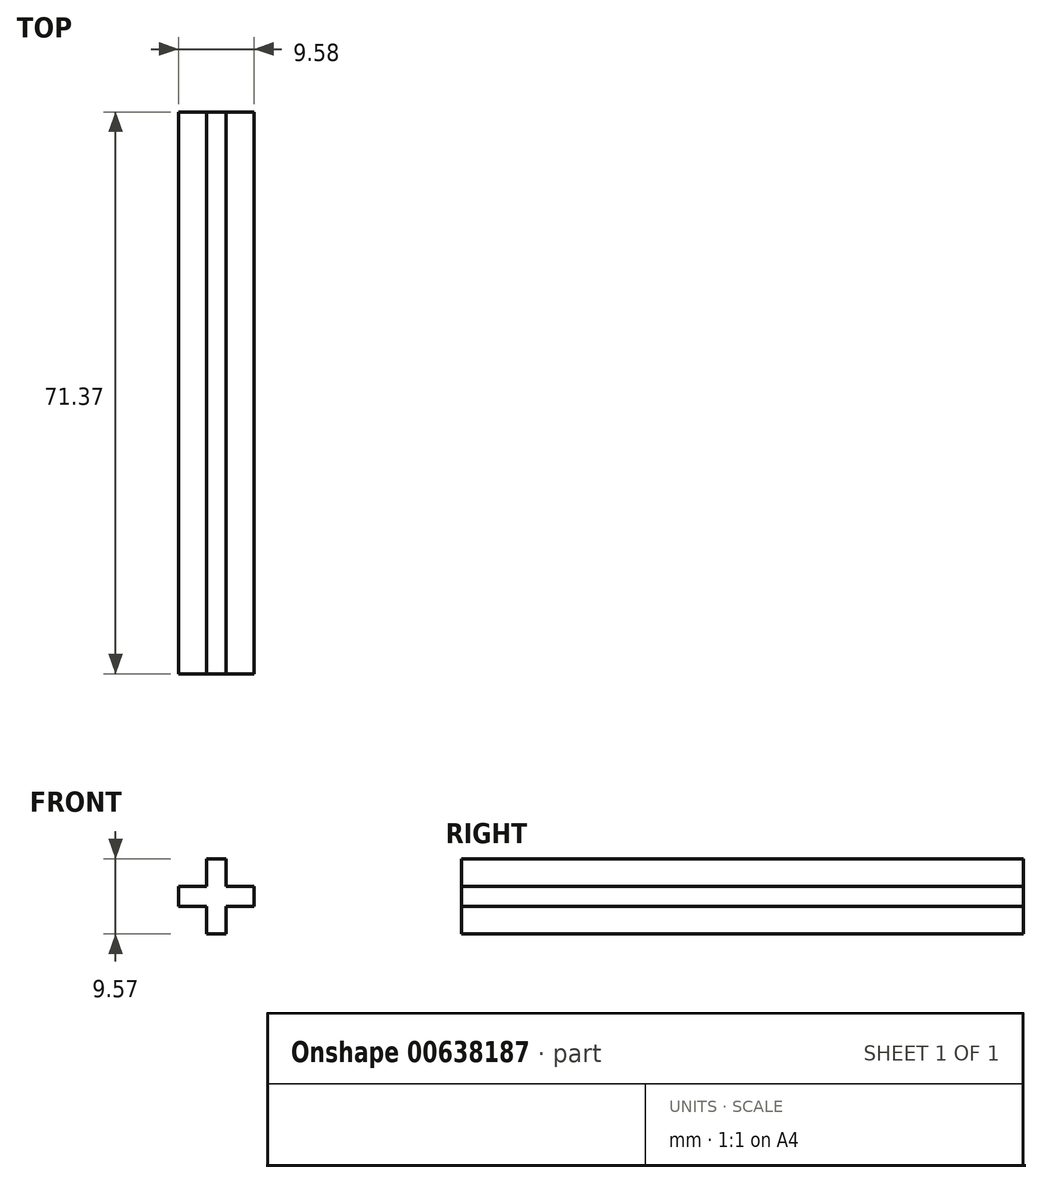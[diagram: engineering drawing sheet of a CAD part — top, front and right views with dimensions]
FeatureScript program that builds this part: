
annotation { "Feature Type Name" : "Feature", "Feature Type Description" : "" }
export const myFeature = defineFeature(function(context is Context, id is Id, definition is map)
    precondition{}
    {
        {
            var Q0;
            Q0=qCreatedBy(makeId("Front.planeOp"),FACE);
            var sketch = newSketch(context, id + "F0", { "sketchPlane" : qUnion([Q0])});
            skLineSegment(sketch, "E0.bottom", {"start": v(0, 0) * mm, "end": v(-2.5, 0) * mm});
            skLineSegment(sketch, "E0.top", {"start": v(0, 9.57) * mm, "end": v(-2.5, 9.57) * mm});
            skLineSegment(sketch, "E0.left", {"start": v(0, 0) * mm, "end": v(0, 3.54) * mm});
            skLineSegment(sketch, "E0.right", {"start": v(-2.5, 0) * mm, "end": v(-2.5, 3.54) * mm});
            skLineSegment(sketch, "E1.bottom", {"start": v(-6.04, 6.04) * mm, "end": v(-2.5, 6.04) * mm});
            skLineSegment(sketch, "E1.top", {"start": v(-6.04, 3.54) * mm, "end": v(-2.5, 3.54) * mm});
            skLineSegment(sketch, "E1.left", {"start": v(-6.04, 6.04) * mm, "end": v(-6.04, 3.54) * mm});
            skLineSegment(sketch, "E1.right", {"start": v(3.54, 6.04) * mm, "end": v(3.54, 3.54) * mm});
            skLineSegment(sketch, "E2.trimOffspring", {"start": v(-2.5, 6.04) * mm, "end": v(-2.5, 9.57) * mm});
            skLineSegment(sketch, "E3.trimOffspring", {"start": v(0, 6.04) * mm, "end": v(3.54, 6.04) * mm});
            skLineSegment(sketch, "E4.trimOffspring", {"start": v(0, 6.04) * mm, "end": v(0, 9.57) * mm});
            skLineSegment(sketch, "E5.trimOffspring", {"start": v(0, 3.54) * mm, "end": v(3.54, 3.54) * mm});
            skSolve(sketch);
        }
        {
            var Q0;
            Q0=makeQuery(id+"F0.imprint","IMPRINT",FACE,{"disambiguationData":[TD([[makeQuery(id+"F0.imprint","IMPRINT",EDGE,{"derivedFrom":sQuery(id+"F0.wireOp",EDGE,"E0.bottom")}),-1.0]])]});
            extrude(context, id + "F1", {"entities" : qUnion([Q0]), "depth" : 71.37 * mm, "offsetDistance" : 25.4 * mm});
        }
    });
